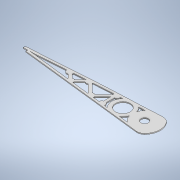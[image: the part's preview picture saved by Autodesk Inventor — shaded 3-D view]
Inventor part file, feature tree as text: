
AUTODESK INVENTOR PART (.ipt)
format: ipt  version: 2022 (Build 260153000, 153)  size: 357,376 bytes
history: native  units: mm
features: extrude x1, sketch x1
ambient origin geometry x8: Origin, YZ Plane, XZ Plane, XY Plane, X Axis, Y Axis, Z Axis, Center Point
bodies: Body1 (feature_tree)
feature tree (2):
  extrude  "Extrusion5"  Depth=1.0mm
  sketch  "Sketch1"  dims[d31=34.456mm d50=368.759386mm d57=16.0mm d69=8.0mm d70=23.0mm d71=8.0mm d73=16.0mm d80=19.0mm d81=16.0mm d82=1.0mm d83=1.0mm d84=1.0mm d85=1.0mm d86=1.0mm d87=0.8mm d88=1.0mm d90=19.0mm d94=5.0mm d95=5.0mm d105=5.0mm d106=5.0mm d108=2.0mm d109=19.0mm d114=5.0mm d115=5.0mm d116=24.0mm d117=2.5mm d118=2.5mm d123=2.5mm d124=2.5mm d125=10.0mm d126=24.0mm d127=24.0mm d128=27.0mm d135=0.5mm d136=45.0deg d139=7.0mm d165=45.0deg d169=27.0mm d175=90.0deg d181=45.0deg d185=7.0mm d186=45.0deg d190=7.0mm d191=45.0deg d197=90.0deg d203=90.0deg d206=7.0mm d207=1.0mm d208=0.0mm]
